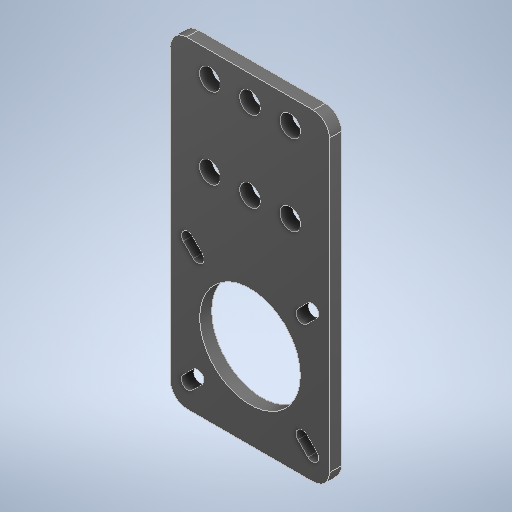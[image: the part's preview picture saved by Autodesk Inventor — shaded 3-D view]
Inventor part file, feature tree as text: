
AUTODESK INVENTOR PART (.ipt)
format: ipt  version: 2025.2 (Build 292293000, 293)  size: 280,064 bytes
history: native  units: in
note: dims shown in document units (in); Inventor stores cm internally (conversion verified against a paired STEP export)
features: plane x1, imported_body x1
ambient origin geometry x8: Origin, YZ Plane, XZ Plane, XY Plane, X Axis, Y Axis, Z Axis, Center Point
bodies: Solid1 (feature_tree)
feature tree (2):
  plane  "Work Plane1"
  imported_body  "Base1"
